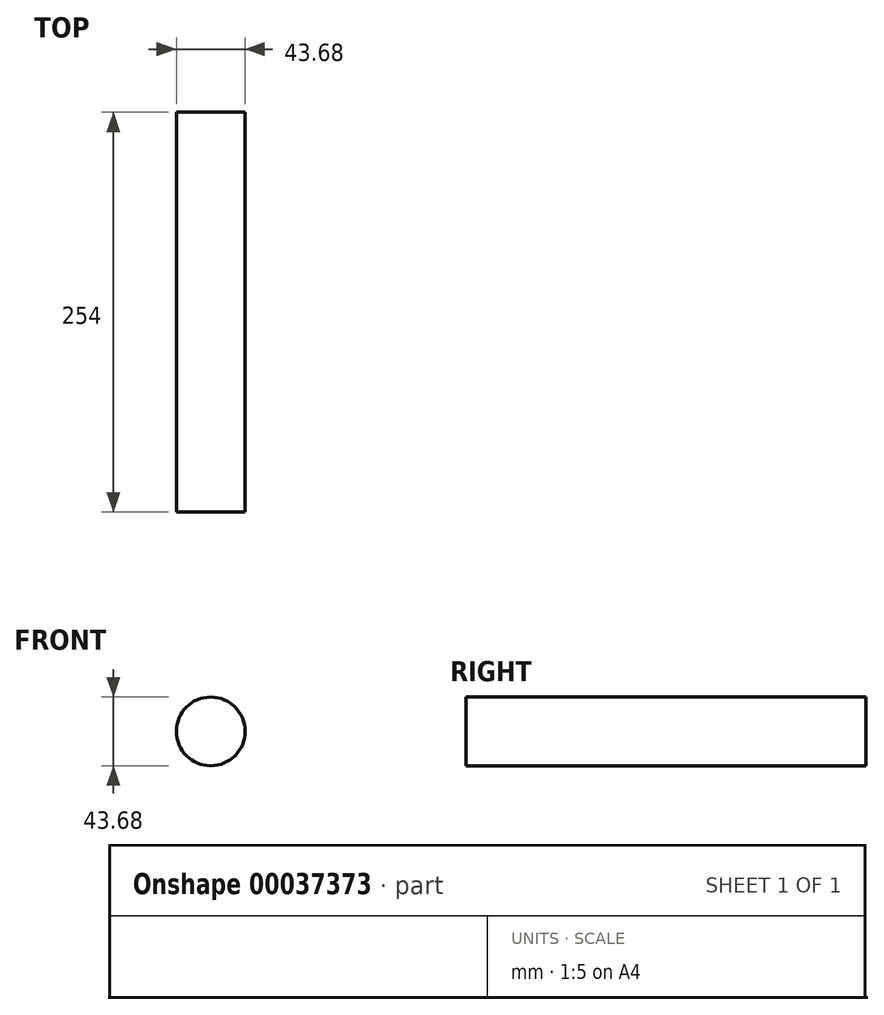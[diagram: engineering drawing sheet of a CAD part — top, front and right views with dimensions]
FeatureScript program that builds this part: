
annotation { "Feature Type Name" : "Feature", "Feature Type Description" : "" }
export const myFeature = defineFeature(function(context is Context, id is Id, definition is map)
    precondition{}
    {
        {
            var Q0;
            Q0=qCreatedBy(makeId("Front.planeOp"),FACE);
            var sketch = newSketch(context, id + "F0", { "sketchPlane" : qUnion([Q0])});
            skCircle(sketch, "E0", {"center": v(0, 0) * mm, "radius": 21.84 * mm});
            skSolve(sketch);
        }
        {
            var Q0;
            Q0=makeQuery(id+"F0.imprint","IMPRINT",FACE,{"disambiguationData":[TD([[makeQuery(id+"F0.imprint","IMPRINT",EDGE,{"derivedFrom":sQuery(id+"F0.wireOp",EDGE,"E0")}),1.0]])]});
            extrude(context, id + "F1", {"entities" : qUnion([Q0]), "depth" : 254 * mm});
        }
    });
